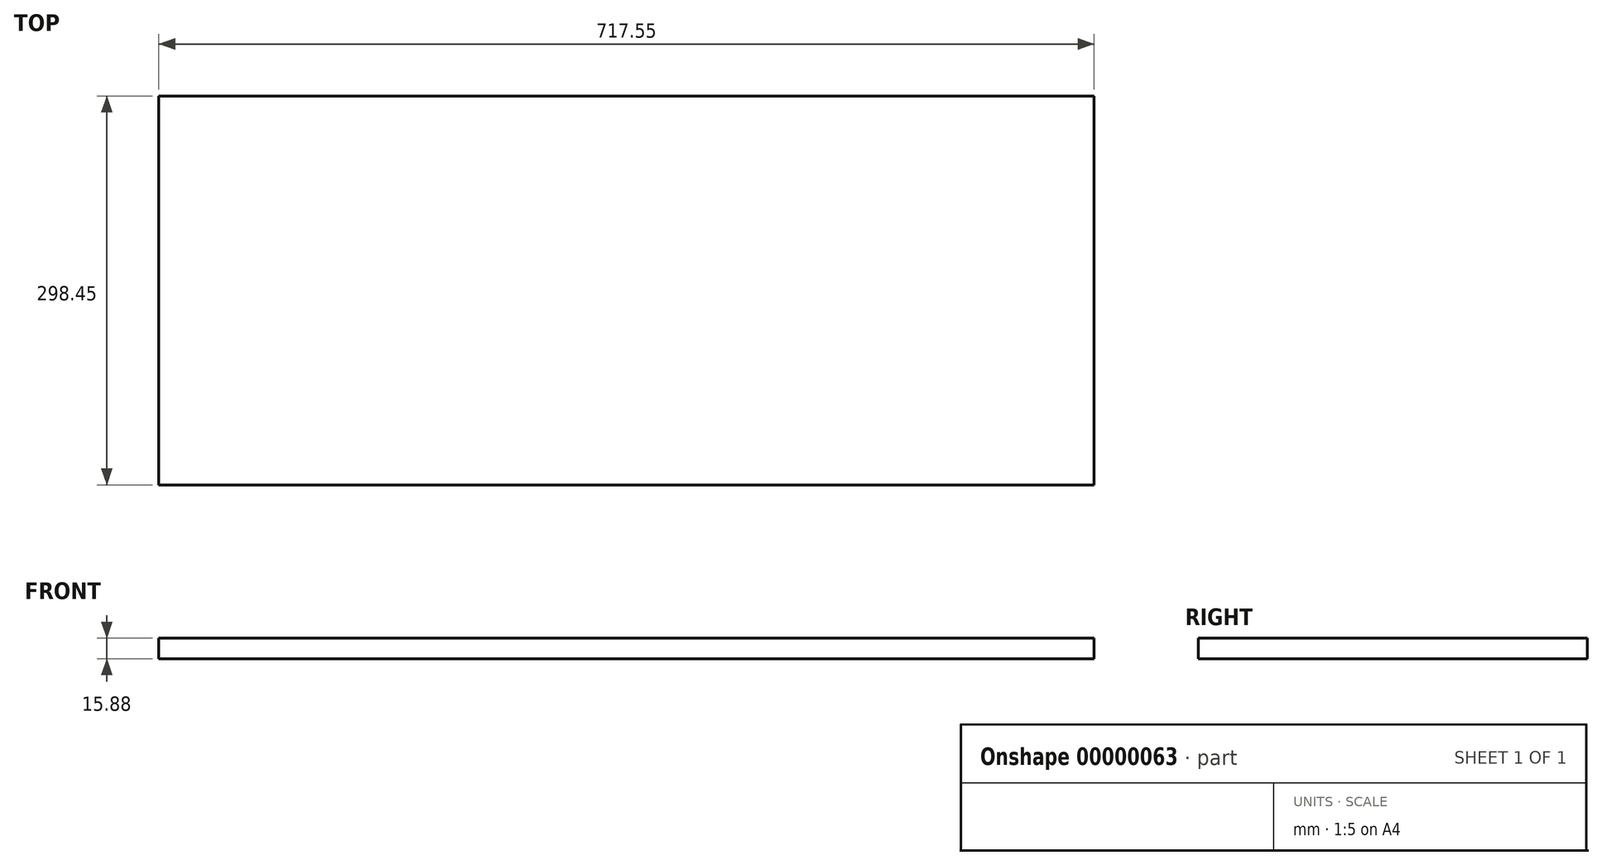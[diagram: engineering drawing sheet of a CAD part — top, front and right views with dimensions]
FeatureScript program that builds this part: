
annotation { "Feature Type Name" : "Feature", "Feature Type Description" : "" }
export const myFeature = defineFeature(function(context is Context, id is Id, definition is map)
    precondition{}
    {
        {
            var Q0;
            Q0=qCreatedBy(makeId("Top.planeOp"),FACE);
            var sketch = newSketch(context, id + "F0", { "sketchPlane" : qUnion([Q0])});
            skLineSegment(sketch, "E0.bottom", {"start": v(0, 0) * mm, "end": v(717.55, 0) * mm});
            skLineSegment(sketch, "E0.top", {"start": v(0, -298.45) * mm, "end": v(717.55, -298.45) * mm});
            skLineSegment(sketch, "E0.left", {"start": v(0, 0) * mm, "end": v(0, -298.45) * mm});
            skLineSegment(sketch, "E0.right", {"start": v(717.55, 0) * mm, "end": v(717.55, -298.45) * mm});
            skSolve(sketch);
        }
        {
            var Q0;
            Q0=makeQuery(id+"F0.imprint","IMPRINT",FACE,{"disambiguationData":[TD([[makeQuery(id+"F0.imprint","IMPRINT",EDGE,{"derivedFrom":sQuery(id+"F0.wireOp",EDGE,"E0.bottom")}),-1.0]])]});
            extrude(context, id + "F1", {"entities" : qUnion([Q0]), "depth" : 15.88 * mm});
        }
    });
